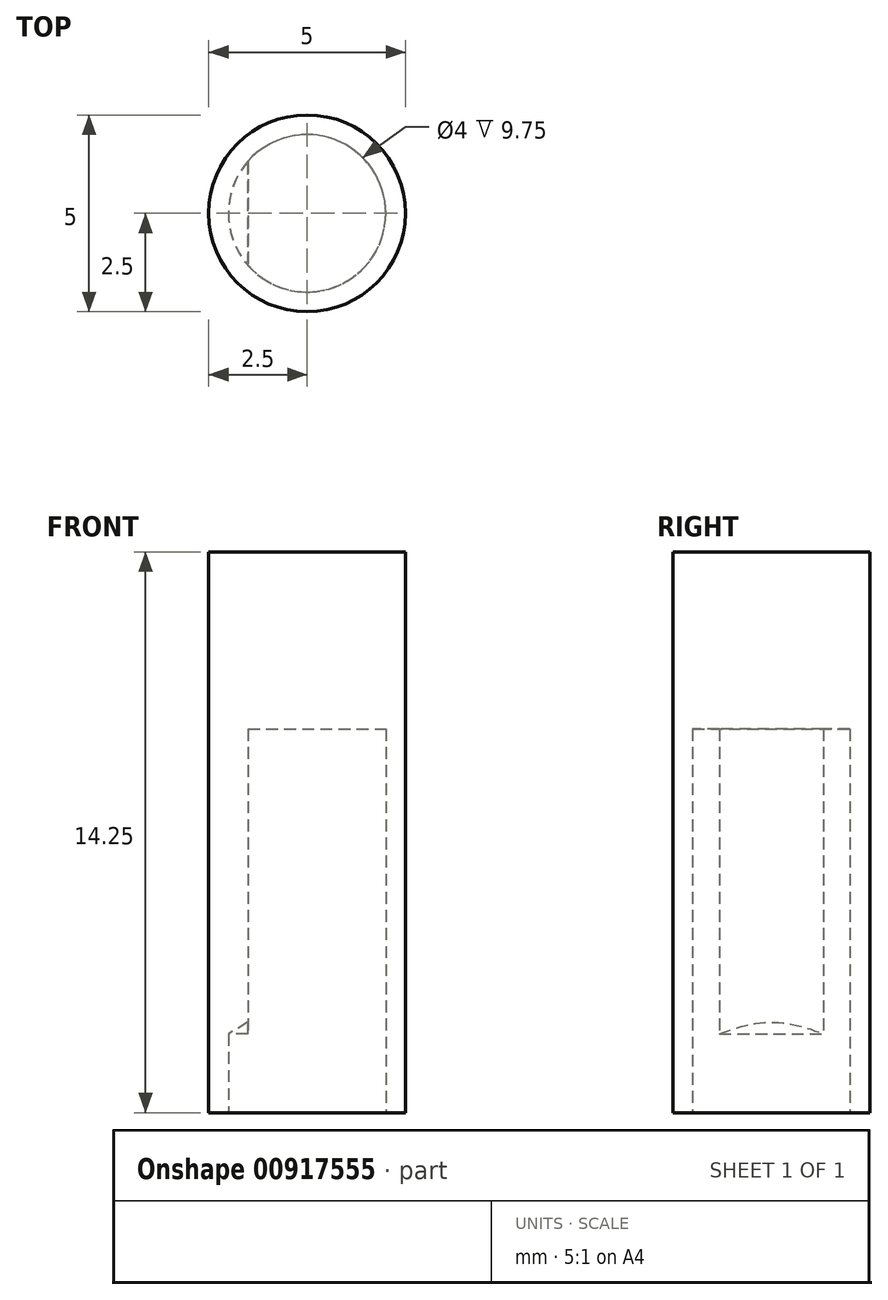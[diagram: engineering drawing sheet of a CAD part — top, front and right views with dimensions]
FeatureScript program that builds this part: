
annotation { "Feature Type Name" : "Feature", "Feature Type Description" : "" }
export const myFeature = defineFeature(function(context is Context, id is Id, definition is map)
    precondition{}
    {
        {
            var Q0;
            Q0=qCreatedBy(makeId("Top.planeOp"),FACE);
            var sketch = newSketch(context, id + "F0", { "sketchPlane" : qUnion([Q0])});
            skCircle(sketch, "E0", {"center": v(0, 0) * mm, "radius": 2.5 * mm});
            skArc(sketch, "E1", {"start": v(-1.5, -1.32) * mm, "mid": v(2, 0) * mm, "end": v(-1.5, 1.32) * mm});
            skLineSegment(sketch, "E2", {"start": v(-1.5, 1.32) * mm, "end": v(-1.5, -1.32) * mm});
            skSolve(sketch);
        }
        {
            var Q0;
            Q0=qSketchRegion(id+"F0",true);
            extrude(context, id + "F1", {"entities" : qUnion([Q0]), "depth" : 14.25 * mm, "offsetDistance" : 25 * mm});
        }
        {
            var Q0;
            Q0=makeQuery(id+"F1.opExtrude","CAP_FACE",FACE,{"disambiguationData":[OSD([sQuery(id+"F0.wireOp",EDGE,"E0"),sQuery(id+"F0.wireOp",EDGE,"E1"),sQuery(id+"F0.wireOp",EDGE,"E2")])],"isStart":true});
            var sketch = newSketch(context, id + "F2", { "sketchPlane" : qUnion([Q0])});
            skPoint(sketch, "E3", {"position": v(0, 0) * mm});
            skSolve(sketch);
        }
        {
            var Q0;
            Q0=sQuery(id+"F2.wireOp",VERTEX,"E3");
            var Q1;
            Q1=makeQuery(id+"F1.opExtrude","SWEPT_BODY",BODY,{"disambiguationData":[OSD([sQuery(id+"F0.wireOp",EDGE,"E0"),sQuery(id+"F0.wireOp",EDGE,"E1"),sQuery(id+"F0.wireOp",EDGE,"E2")])]});
            hole(context, id + "F3", {"style" : HoleStyle.SIMPLE, "endStyle" : HoleEndStyle.BLIND, "holeDiameter" : 4 * mm, "majorDiameter" : 6.35 * mm, "holeDepth" : 2 * mm, "isTappedThrough" : true, "tappedDepth" : 12 * mm, "tapClearance" : 3, "locations" : qUnion([Q0]), "scope" : qUnion([Q1])});
        }
        {
            var Q0;
            Q0=makeQuery(id+"F1.opExtrude","CAP_FACE",FACE,{"disambiguationData":[OSD([sQuery(id+"F0.wireOp",EDGE,"E0"),sQuery(id+"F0.wireOp",EDGE,"E1"),sQuery(id+"F0.wireOp",EDGE,"E2")])],"isStart":false});
            var sketch = newSketch(context, id + "F4", { "sketchPlane" : qUnion([Q0])});
            skCircle(sketch, "E4", {"center": v(0, 0) * mm, "radius": 2.15 * mm});
            skSolve(sketch);
        }
        {
            var Q0;
            Q0=makeQuery(id+"F4.imprint","IMPRINT",FACE,{"disambiguationData":[TD([[makeQuery(id+"F4.imprint","IMPRINT",EDGE,{"derivedFrom":sQuery(id+"F4.wireOp",EDGE,"E4")}),1.0]])]});
            var Q1;
            Q1=makeQuery(id+"F4.imprint","IMPRINT",FACE,{"disambiguationData":[TD([[makeQuery(id+"F4.imprint","IMPRINT",EDGE,{"derivedFrom":makeQuery(id+"F1.opExtrude","CAP_EDGE",EDGE,{"disambiguationData":[OSD([sQuery(id+"F0.wireOp",EDGE,"E1")])],"isStart":false})}),1.0]])]});
            var Q2;
            Q2=sQuery(id+"F4.wireOp",EDGE,"E4");
            extrude(context, id + "F5", {"entities" : qUnion([Q0, Q1]), "operationType" : NewBodyOperationType.ADD, "surfaceOperationType" : NewSurfaceOperationType.ADD, "surfaceEntities" : qUnion([Q2]), "oppositeDirection" : true, "depth" : 4.5 * mm, "offsetDistance" : 25 * mm});
        }
    });
